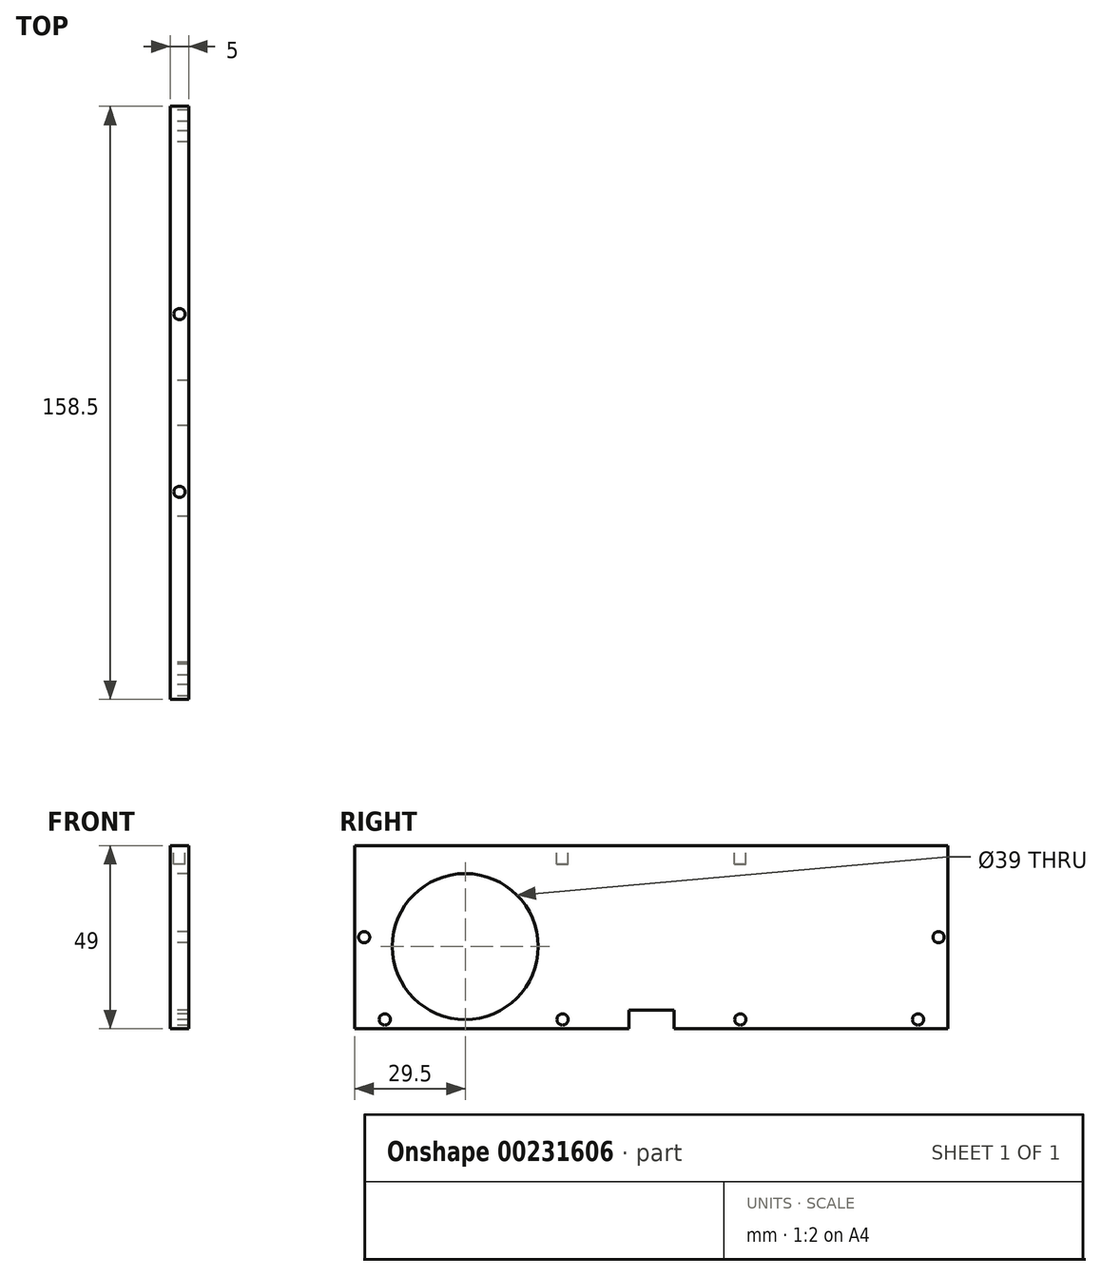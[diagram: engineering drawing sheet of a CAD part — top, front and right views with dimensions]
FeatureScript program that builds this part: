
annotation { "Feature Type Name" : "Feature", "Feature Type Description" : "" }
export const myFeature = defineFeature(function(context is Context, id is Id, definition is map)
    precondition{}
    {
        {
            var Q0;
            Q0=qCreatedBy(makeId("Right.planeOp"),FACE);
            var sketch = newSketch(context, id + "F0", { "sketchPlane" : qUnion([Q0])});
            skLineSegment(sketch, "E0.bottom", {"start": v(0, 0) * mm, "end": v(73.25, 0) * mm});
            skLineSegment(sketch, "E0.top", {"start": v(0, 49) * mm, "end": v(158.5, 49) * mm});
            skLineSegment(sketch, "E0.left", {"start": v(0, 0) * mm, "end": v(0, 49) * mm});
            skLineSegment(sketch, "E0.right", {"start": v(158.5, 0) * mm, "end": v(158.5, 49) * mm});
            skLineSegment(sketch, "E1", {"start": v(0, 2.5) * mm, "end": v(158.5, 2.5) * mm, "construction": true});
            skCircle(sketch, "E2", {"center": v(8, 2.5) * mm, "radius": 1.5 * mm});
            skCircle(sketch, "E3", {"center": v(55.5, 2.5) * mm, "radius": 1.5 * mm});
            skCircle(sketch, "E4", {"center": v(103, 2.5) * mm, "radius": 1.5 * mm});
            skCircle(sketch, "E5", {"center": v(150.5, 2.5) * mm, "radius": 1.5 * mm});
            skCircle(sketch, "E6", {"center": v(2.5, 24.5) * mm, "radius": 1.5 * mm});
            skCircle(sketch, "E7", {"center": v(156, 24.5) * mm, "radius": 1.5 * mm});
            skLineSegment(sketch, "E8.top", {"start": v(73.25, 5) * mm, "end": v(85.25, 5) * mm});
            skLineSegment(sketch, "E8.left", {"start": v(73.25, 0) * mm, "end": v(73.25, 5) * mm});
            skLineSegment(sketch, "E8.right", {"start": v(85.25, 0) * mm, "end": v(85.25, 5) * mm});
            skPoint(sketch, "E9", {"position": v(79.25, 49) * mm});
            skLineSegment(sketch, "E10", {"start": v(79.25, 49) * mm, "end": v(79.25, 0) * mm, "construction": true});
            skPoint(sketch, "E11", {"position": v(79.25, 5) * mm});
            skLineSegment(sketch, "E12.trimOffspring", {"start": v(85.25, 0) * mm, "end": v(158.5, 0) * mm});
            skCircle(sketch, "E13", {"center": v(29.5, 22) * mm, "radius": 19.5 * mm});
            skSolve(sketch);
        }
        {
            var Q0;
            Q0 = qSketchRegion(id + "F0", true);
            extrude(context, id + "F1", {"entities" : qUnion([Q0]), "depth" : 5 * mm});
        }
        {
            var Q0;
            Q0=makeQuery(id+"F1.opExtrude","SWEPT_FACE",FACE,{"disambiguationData":[OSD([sQuery(id+"F0.wireOp",EDGE,"E0.top")])]});
            var sketch = newSketch(context, id + "F2", { "sketchPlane" : qUnion([Q0])});
            skLineSegment(sketch, "E14", {"start": v(2.5, 0) * mm, "end": v(2.5, 158.5) * mm, "construction": true});
            skCircle(sketch, "E15", {"center": v(2.5, 8) * mm, "radius": 1.5 * mm, "construction": true});
            skCircle(sketch, "E16", {"center": v(2.5, 55.5) * mm, "radius": 1.5 * mm});
            skCircle(sketch, "E17", {"center": v(2.5, 103) * mm, "radius": 1.5 * mm});
            skCircle(sketch, "E18", {"center": v(2.5, 150.5) * mm, "radius": 1.5 * mm, "construction": true});
            skSolve(sketch);
        }
        {
            var Q0;
            Q0 = qSketchRegion(id + "F2", true);
            extrude(context, id + "F3", {"entities" : qUnion([Q0]), "operationType" : NewBodyOperationType.REMOVE, "oppositeDirection" : true, "depth" : 5 * mm});
        }
    });
